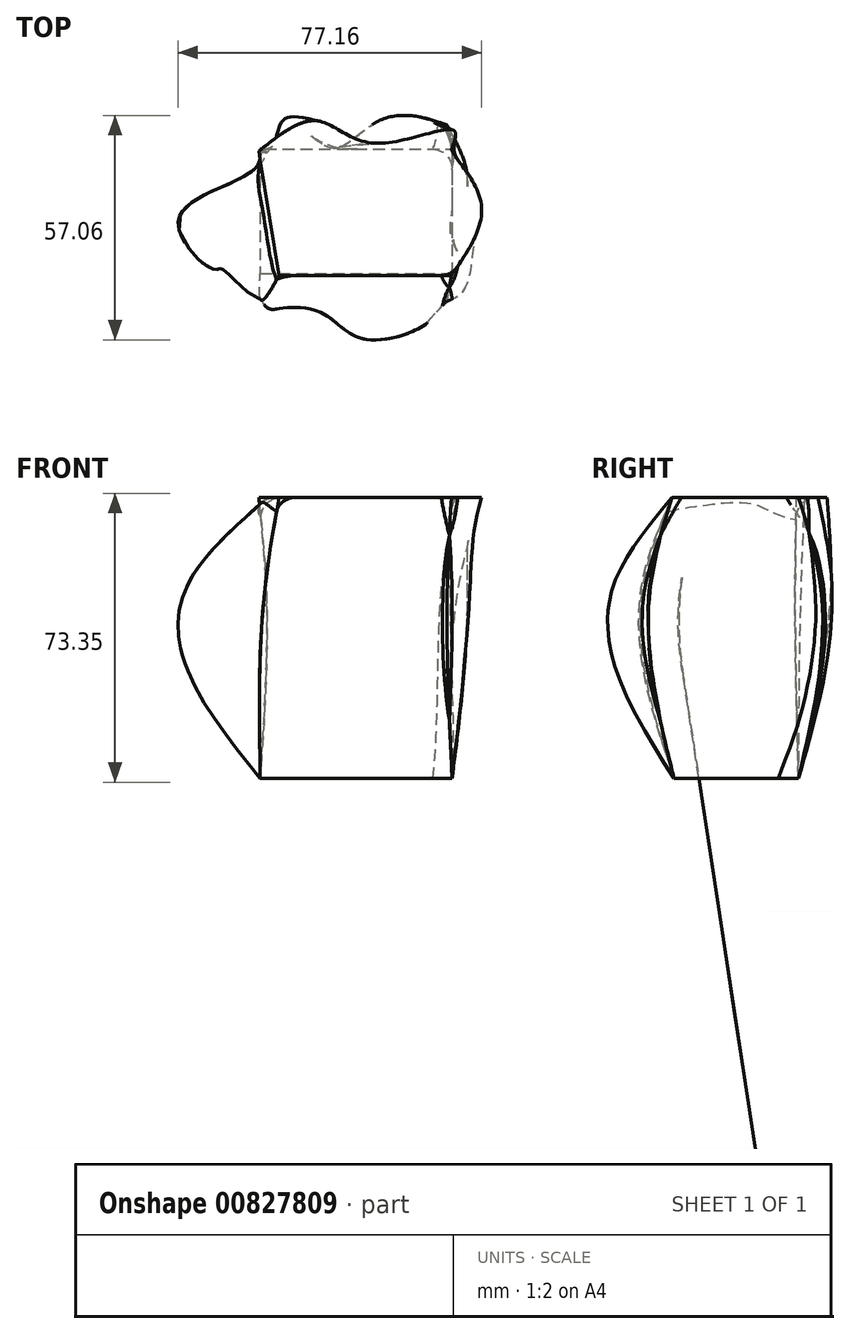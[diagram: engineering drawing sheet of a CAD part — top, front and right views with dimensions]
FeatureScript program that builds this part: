
annotation { "Feature Type Name" : "Feature", "Feature Type Description" : "" }
export const myFeature = defineFeature(function(context is Context, id is Id, definition is map)
    precondition{}
    {
        {
            var Q0;
            Q0=qCreatedBy(makeId("Top.planeOp"),FACE);
            cPlane(context, id + "F0", {"entities" : qUnion([Q0]), "cplaneType" : CPlaneType.OFFSET, "offset" : 50.3 * mm, "width" : 152.4 * mm, "height" : 152.4 * mm});
        }
        {
            var Q0;
            Q0=qCreatedBy(id+"F0.planeOp",FACE);
            cPlane(context, id + "F1", {"entities" : qUnion([Q0]), "cplaneType" : CPlaneType.OFFSET, "offset" : 21.08 * mm, "width" : 152.4 * mm, "height" : 152.4 * mm});
        }
        {
            var Q0;
            Q0=qCreatedBy(makeId("Top.planeOp"),FACE);
            var sketch = newSketch(context, id + "F2", { "sketchPlane" : qUnion([Q0])});
            skLineSegment(sketch, "E0.bottom", {"start": v(-13, 8.11) * mm, "end": v(35.76, 8.11) * mm});
            skLineSegment(sketch, "E0.top", {"start": v(-13, -23.48) * mm, "end": v(35.76, -23.48) * mm});
            skLineSegment(sketch, "E0.left", {"start": v(-13, 8.11) * mm, "end": v(-13, -23.48) * mm});
            skLineSegment(sketch, "E0.right", {"start": v(35.76, 8.11) * mm, "end": v(35.76, -23.48) * mm});
            skSolve(sketch);
        }
        {
            var Q0;
            Q0=qCreatedBy(id+"F0.planeOp",FACE);
            var sketch = newSketch(context, id + "F3", { "sketchPlane" : qUnion([Q0])});
            skFitSpline(sketch, "E1", {"points": [v(-11.56, 7.27) * mm, v(-7.17, 15.15) * mm, v(-3.4, 15.95) * mm, v(6.74, 8.8) * mm, v(20.3, 15.67) * mm, v(34.56, 13.52) * mm], "startDerivative": vector(46.01, 44.13) * mm, "endDerivative": vector(61.4, -33.64) * mm});
            skFitSpline(sketch, "E2", {"points": [v(34.56, 13.52) * mm, v(39.7, 0) * mm, v(37.64, -11.8) * mm, v(40.4, -21.6) * mm, v(34.56, -29.48) * mm], "startDerivative": vector(22.87, -39.87) * mm, "endDerivative": vector(-47.86, -5.14) * mm});
            skFitSpline(sketch, "E3", {"points": [v(34.56, -29.48) * mm, v(30.09, -33.78) * mm, v(28.89, -34.81) * mm, v(22.2, -37.56) * mm, v(11.55, -37.56) * mm, v(2.96, -32.24) * mm, v(-7, -31.38) * mm, v(-11.56, -29.48) * mm], "startDerivative": vector(-34.96, -40.27) * mm, "endDerivative": vector(-35.28, 64) * mm});
            skFitSpline(sketch, "E4", {"points": [v(-11.56, -29.48) * mm, v(-20.73, -21.76) * mm, v(-22.8, -21.42) * mm, v(-30.86, -9.92) * mm, v(-18.67, 0) * mm, v(-11.56, 7.27) * mm], "startDerivative": vector(-47.06, 13.94) * mm, "endDerivative": vector(12.1, 44.94) * mm});
            skSolve(sketch);
        }
        {
            var Q0;
            Q0=qCreatedBy(id+"F1.planeOp",FACE);
            var sketch = newSketch(context, id + "F4", { "sketchPlane" : qUnion([Q0])});
            skFitSpline(sketch, "E5", {"points": [v(-13.35, 7.6) * mm, v(1.42, 15.32) * mm, v(15.67, 9.66) * mm, v(36.1, 12.92) * mm, v(35.58, 8.11) * mm], "startDerivative": vector(55.74, 44.52) * mm, "endDerivative": vector(-16.66, -42.21) * mm});
            skFitSpline(sketch, "E6", {"points": [v(35.58, 8.11) * mm, v(36.44, 6.4) * mm, v(43.14, -5.62) * mm, v(35.58, -24) * mm], "startDerivative": vector(3.11, -9.29) * mm, "endDerivative": vector(-27.36, -39.8) * mm});
            skLineSegment(sketch, "E7", {"start": v(35.58, -24) * mm, "end": v(-8.2, -24) * mm});
            skLineSegment(sketch, "E8", {"start": v(-8.2, -24) * mm, "end": v(-13.35, 7.6) * mm});
            skSolve(sketch);
        }
        {
            var Q0;
            Q0 = qSketchRegion(id + "F4", true);
            var Q1;
            Q1 = qSketchRegion(id + "F3", true);
            var Q2;
            Q2 = qSketchRegion(id + "F2", true);
            loft(context, id + "F5", {"sheetProfilesArray" : [{ "sheetProfileEntities" : qUnion([Q0]) }, { "sheetProfileEntities" : qUnion([Q1]) }, { "sheetProfileEntities" : qUnion([Q2]) }]});
        }
        {
            var Q0;
            Q0 = qSketchRegion(id + "F2", true);
            var Q1;
            Q1 = qSketchRegion(id + "F3", true);
            var Q2;
            Q2 = qSketchRegion(id + "F4", true);
            loft(context, id + "F6", {"sheetProfilesArray" : [{ "sheetProfileEntities" : qUnion([Q0]) }, { "sheetProfileEntities" : qUnion([Q1]) }, { "sheetProfileEntities" : qUnion([Q2]) }]});
        }
        {
            var Q0;
            Q0=makeQuery(id+"F5.opLoft","SWEPT_EDGE",EDGE,{"disambiguationData":[OSD([sQuery(id+"F2.wireOp",EDGE,"E0.bottom"),sQuery(id+"F2.wireOp",EDGE,"E0.right"),sQuery(id+"F3.wireOp",EDGE,"E1"),sQuery(id+"F3.wireOp",EDGE,"E2"),sQuery(id+"F4.wireOp",EDGE,"E5"),sQuery(id+"F4.wireOp",EDGE,"E6")])]});
            fillet(context, id + "F7", {"entities" : qUnion([Q0]), "radius" : 5.08 * mm, "tangentPropagation" : true, "allowEdgeOverflow" : false});
        }
        {
            var Q0;
            Q0=makeQuery(id+"F5.opLoft","SWEPT_EDGE",EDGE,{"disambiguationData":[OSD([sQuery(id+"F2.wireOp",EDGE,"E0.top"),sQuery(id+"F2.wireOp",EDGE,"E0.right"),sQuery(id+"F3.wireOp",EDGE,"E2"),sQuery(id+"F3.wireOp",EDGE,"E3"),sQuery(id+"F4.wireOp",EDGE,"E6"),sQuery(id+"F4.wireOp",EDGE,"E7")])]});
            fillet(context, id + "F8", {"entities" : qUnion([Q0]), "radius" : 5.08 * mm, "tangentPropagation" : true, "allowEdgeOverflow" : false});
        }
        {
            var Q0;
            Q0=makeQuery(id+"F5.opLoft","MID_CAP_EDGE",EDGE,{"disambiguationData":[OSD([sQuery(id+"F4.wireOp",EDGE,"E5"),sQuery(id+"F4.wireOp",EDGE,"E7"),sQuery(id+"F4.wireOp",EDGE,"E8")])],"capPos":0.0});
            fillet(context, id + "F9", {"entities" : qUnion([Q0]), "radius" : 5.08 * mm, "tangentPropagation" : true, "allowEdgeOverflow" : false});
        }
    });
